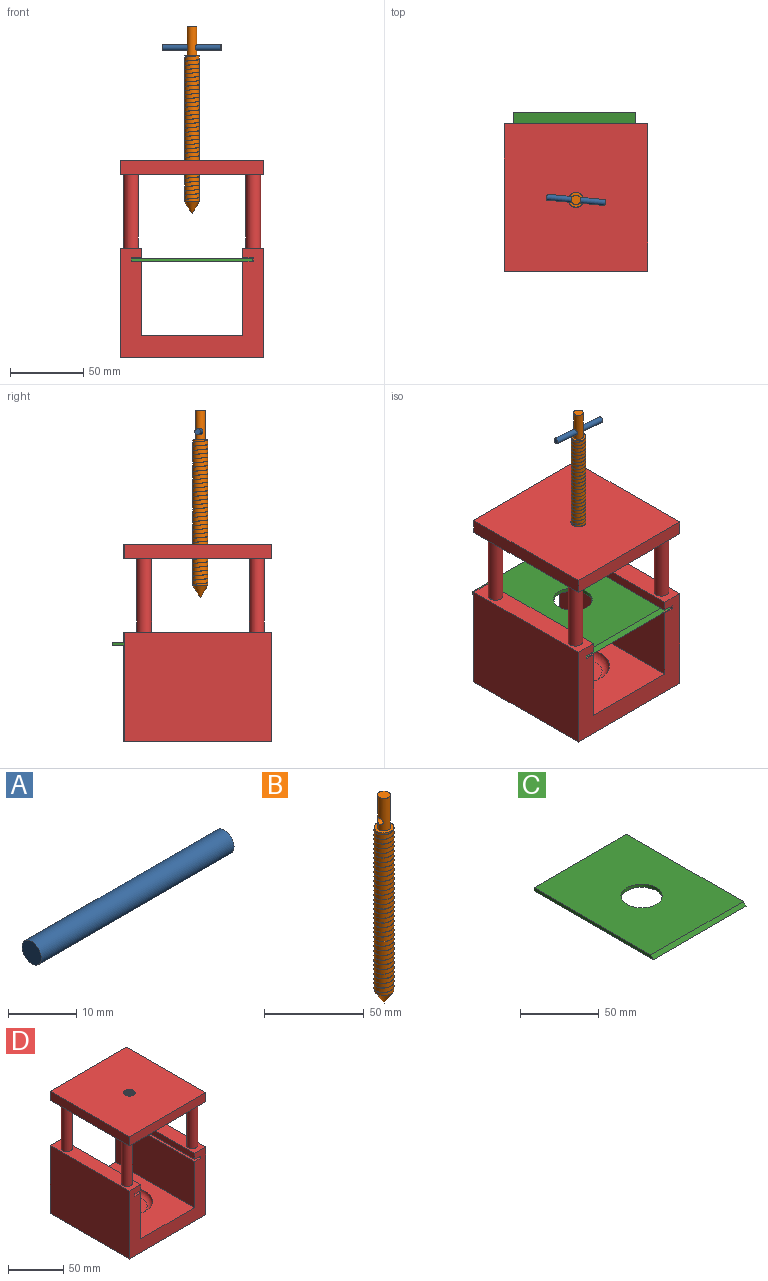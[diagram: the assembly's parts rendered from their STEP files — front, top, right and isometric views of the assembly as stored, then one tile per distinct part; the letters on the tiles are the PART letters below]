
ASSEMBLY  parts=4 mates=3
PART A: 3 faces, bbox 40x4x4 mm
  f0: cylinder r=2mm len=40mm, axis (-1,0,0), area 502.7mm2, adj f1,f2
  f1: plane 4x4mm, normal (1,0,0), area 12.6mm2, adj f0
  f2: plane 4x4mm, normal (-1,0,0), area 12.6mm2, adj f0
PART B: 11 faces, bbox 10.2x11.7x128 mm
  f0: cylinder r=5mm len=100mm, axis (0,0,-1), area 3221.5mm2, adj f1,f2,f6,f8,f9
  f1: plane 10x10mm, normal (0,0,1), area 45.3mm2, adj f0,f3,f5
  f2: cone r=0mm half-angle=31.9deg, axis (0,0,1), area 148.7mm2, adj f0
  f3: cylinder r=3.25mm len=20mm, axis (0,0,-1), area 382.4mm2, adj f1,f4,f10
  f4: plane 6.51x6.51mm, normal (0,0,1), area 33.3mm2, adj f3
  f5: cylinder r=5mm len=1.14mm, axis (0,0,1), area 0.1mm2, adj f1,f7,f9
  f6: plane 0.1x0.09mm, normal (0,-1,0), area 0mm2, adj f0,f8,f9
  f7: plane 0.1x0.09mm, normal (0,1,0), area 0mm2, adj f5,f8,f9
  f8: bspline ~100.05x11.75mm, area 111.7mm2, adj f0,f6,f7,f9
  f9: bspline ~100.05x11.75mm, area 111.7mm2, adj f0,f5,f6,f7,f8
  f10: cylinder r=2mm len=6.51mm, axis (1,0,0), area 81.8mm2, adj f3
PART C: 7 faces, bbox 83.4x107.5x2.5 mm
  f0: plane 83.36x2.5mm, normal (0,1,0), area 208.4mm2, adj f1,f2,f3,f4
  f1: plane 107.5x2.5mm, normal (-1,0,0), area 265.6mm2, adj f0,f3,f4,f5
  f2: plane 107.5x2.5mm, normal (1,0,0), area 265.6mm2, adj f0,f3,f4,f5
  f3: plane 105x83.36mm, normal (0,0,1), area 8209.3mm2, adj f0,f1,f2,f5,f6
  f4: plane 107.5x83.36mm, normal (0,0,-1), area 8417.7mm2, adj f0,f1,f2,f5,f6
  f5: plane 83.36x2.5mm, normal (0,-0.71,0.71), area 294.7mm2, adj f1,f2,f3,f4
  f6: cylinder r=13.15mm len=26.31mm, axis (0,0,1), area 206.6mm2, adj f3,f4
PART D: 69 faces, bbox 97.9x101x135.1 mm
  f0: plane 97.85x75mm, normal (0,1,0), area 3170.1mm2, adj f2,f3,f4,f5,f6,f7,f8,f9
  f1: plane 97.85x75mm, normal (0,-1,0), area 3170.1mm2, adj f2,f3,f4,f5,f6,f7,f8,f9
  f2: plane 100.92x6.61mm, normal (1,0,0), area 666.6mm2, adj f0,f1,f8,f22
  f3: plane 100.92x6.61mm, normal (-1,0,0), area 666.6mm2, adj f0,f1,f9,f19
  f4: plane 100.92x68.88mm, normal (0,0,1), area 5552mm2, adj f0,f1,f7,f11,f12
  f5: plane 100.92x75mm, normal (-1,0,0), area 7569.3mm2, adj f0,f1,f6,f8
  f6: plane 100.92x97.85mm, normal (0,0,-1), area 9875.7mm2, adj f0,f1,f5,f13
  f7: plane 100.92x50.89mm, normal (1,0,0), area 5136.5mm2, adj f0,f1,f4,f23
  f8: plane 100.92x14.49mm, normal (0,0,1), area 1305.9mm2, adj f0,f1,f2,f5,f14,f16
  f9: plane 100.92x14.49mm, normal (0,0,1), area 1305.9mm2, adj f0,f1,f3,f13,f15,f17
  f10: plane 32.21x32.21mm, normal (0,0,1), area 814.9mm2, adj f11
  f11: torus R=16.11mm, axis (0,0,1), area 951.9mm2, adj f4,f10
  f12: plane 100.92x50.89mm, normal (-1,0,0), area 5136.5mm2, adj f0,f1,f4,f18
  f13: plane 100.92x75mm, normal (1,0,0), area 7569.3mm2, adj f0,f1,f6,f9
  f14: cylinder r=4.99mm len=50mm, axis (0,0,-1), area 1566.5mm2, adj f8,f24
  f15: cylinder r=4.99mm len=50mm, axis (0,0,-1), area 1566.5mm2, adj f9,f24
  f16: cylinder r=4.99mm len=50mm, axis (0,0,-1), area 1566.5mm2, adj f8,f24
  f17: cylinder r=4.99mm len=50mm, axis (0,0,-1), area 1566.5mm2, adj f9,f24
  f18: plane 100.92x7.24mm, normal (0,0,1), area 731.1mm2, adj f0,f1,f12,f20
  f19: plane 100.92x7.24mm, normal (0,0,-1), area 731.1mm2, adj f0,f1,f3,f20
  f20: plane 100.92x2.5mm, normal (-1,0,0), area 252.3mm2, adj f0,f1,f18,f19
  f21: plane 100.92x2.5mm, normal (1,0,0), area 252.3mm2, adj f0,f1,f22,f23
  f22: plane 100.92x7.24mm, normal (0,0,-1), area 731.1mm2, adj f0,f1,f2,f21
  f23: plane 100.92x7.24mm, normal (0,0,1), area 731.1mm2, adj f0,f1,f7,f21
  f24: plane 100.92x97.85mm, normal (0,0,-1), area 9483.2mm2, adj f14,f15,f16,f17,f25,f26,f27,f28
  f25: plane 97.85x10mm, normal (0,1,0), area 978.5mm2, adj f24,f26,f28,f29
  f26: plane 100.92x10mm, normal (-1,0,0), area 1009.2mm2, adj f24,f25,f27,f29
  f27: plane 97.85x10mm, normal (0,-1,0), area 978.5mm2, adj f24,f26,f28,f29
  f28: plane 100.92x10mm, normal (1,0,0), area 1009.2mm2, adj f24,f25,f27,f29
  f29: plane 100.99x97.92mm, normal (0,0,1), area 9795.1mm2, adj f25,f26,f27,f28,f30,f31,f67,f68
  f30: cylinder r=5.05mm len=10.1mm, axis (0,0,1), area 1.7mm2, adj f29,f31,f68
  f31: cylinder r=5.05mm len=10.1mm, axis (0,0,1), area 5.9mm2, adj f29,f30,f32,f67,f68
  f32: cylinder r=5.05mm len=10.1mm, axis (0,0,1), area 5.9mm2, adj f31,f33,f67,f68
  f33: cylinder r=5.05mm len=10.1mm, axis (0,0,1), area 5.9mm2, adj f32,f34,f67,f68
  f34: cylinder r=5.05mm len=10.1mm, axis (0,0,1), area 5.9mm2, adj f33,f35,f67,f68
  f35: cylinder r=5.05mm len=10.1mm, axis (0,0,1), area 5.9mm2, adj f34,f36,f67,f68
  f36: cylinder r=5.05mm len=10.1mm, axis (0,0,1), area 5.9mm2, adj f35,f37,f67,f68
  f37: cylinder r=5.05mm len=10.1mm, axis (0,0,1), area 5.9mm2, adj f36,f38,f67,f68
  f38: cylinder r=5.05mm len=10.1mm, axis (0,0,1), area 5.9mm2, adj f37,f39,f67,f68
  f39: cylinder r=5.05mm len=10.1mm, axis (0,0,1), area 5.9mm2, adj f38,f40,f67,f68
  f40: cylinder r=5.05mm len=10.1mm, axis (0,0,1), area 5.9mm2, adj f39,f41,f67,f68
  f41: cylinder r=5.05mm len=10.1mm, axis (0,0,1), area 5.9mm2, adj f40,f42,f67,f68
  f42: cylinder r=5.05mm len=10.1mm, axis (0,0,1), area 5.9mm2, adj f41,f43,f67,f68
  f43: cylinder r=5.05mm len=10.1mm, axis (0,0,1), area 5.9mm2, adj f42,f44,f67,f68
  f44: cylinder r=5.05mm len=10.1mm, axis (0,0,1), area 5.9mm2, adj f43,f45,f67,f68
  f45: cylinder r=5.05mm len=10.1mm, axis (0,0,1), area 5.9mm2, adj f44,f46,f67,f68
  f46: cylinder r=5.05mm len=10.1mm, axis (0,0,1), area 5.9mm2, adj f45,f47,f67,f68
  f47: cylinder r=5.05mm len=10.1mm, axis (0,0,1), area 5.9mm2, adj f46,f48,f67,f68
  f48: cylinder r=5.05mm len=10.1mm, axis (0,0,1), area 5.9mm2, adj f47,f49,f67,f68
  f49: cylinder r=5.05mm len=10.1mm, axis (0,0,1), area 5.9mm2, adj f48,f50,f67,f68
  f50: cylinder r=5.05mm len=10.1mm, axis (0,0,1), area 5.9mm2, adj f49,f51,f67,f68
  f51: cylinder r=5.05mm len=10.1mm, axis (0,0,1), area 5.9mm2, adj f50,f52,f67,f68
  f52: cylinder r=5.05mm len=10.1mm, axis (0,0,1), area 5.9mm2, adj f51,f53,f67,f68
  f53: cylinder r=5.05mm len=10.1mm, axis (0,0,1), area 5.9mm2, adj f52,f54,f67,f68
  f54: cylinder r=5.05mm len=10.1mm, axis (0,0,1), area 5.9mm2, adj f53,f55,f67,f68
  f55: cylinder r=5.05mm len=10.1mm, axis (0,0,1), area 5.9mm2, adj f54,f56,f67,f68
  f56: cylinder r=5.05mm len=10.1mm, axis (0,0,1), area 5.9mm2, adj f55,f57,f67,f68
  f57: cylinder r=5.05mm len=10.1mm, axis (0,0,1), area 5.9mm2, adj f56,f58,f67,f68
  f58: cylinder r=5.05mm len=10.1mm, axis (0,0,1), area 5.9mm2, adj f57,f59,f67,f68
  f59: cylinder r=5.05mm len=10.1mm, axis (0,0,1), area 5.9mm2, adj f58,f60,f67,f68
  f60: cylinder r=5.05mm len=10.1mm, axis (0,0,1), area 5.9mm2, adj f59,f61,f67,f68
  f61: cylinder r=5.05mm len=10.1mm, axis (0,0,1), area 5.9mm2, adj f60,f62,f67,f68
  f62: cylinder r=5.05mm len=10.1mm, axis (0,0,1), area 5.9mm2, adj f61,f63,f67,f68
  f63: cylinder r=5.05mm len=10.1mm, axis (0,0,1), area 5.9mm2, adj f62,f64,f67,f68
  f64: cylinder r=5.05mm len=10.1mm, axis (0,0,1), area 5.9mm2, adj f63,f65,f67,f68
  f65: cylinder r=5.05mm len=10.1mm, axis (0,0,1), area 4.9mm2, adj f24,f64,f66,f67
  f66: plane 0.1x0.09mm, normal (0,1,0), area 0mm2, adj f65,f67,f68
  f67: bspline ~11.86x10.27mm, area 111.6mm2, adj f29,f31,f32,f33,f34,f35,f36,f37
  f68: bspline ~11.86x10.27mm, area 110.9mm2, adj f29,f30,f31,f32,f33,f34,f35,f36
PLACE A rot(axis=(-1,0.05,-0.05),90.1deg) t=(-112.64,-46.71,175.04)mm
PLACE B rot(axis=(0,0,-1),5.3deg) t=(-112.64,-46.71,69.71)mm
PLACE C rot(axis=(0,0,1),0.2deg) t=(-112.99,-41.62,28.84)mm
PLACE D rot(axis=(0,0,1),0.2deg) t=(-112.64,-46.71,-36.81)mm fixed
MATE cylindrical D.f30 <-> B.f0  axis (0,0,1) through (-112.64,-46.71,93.19)mm
MATE fastened A.f0 <-> B.f10  axis (-1,0.09,0) through (-112.64,-46.71,175.04)mm
MATE slider C.f0 <-> D.f0  axis (0,1,0) through (-113.39,13.38,30.09)mm
